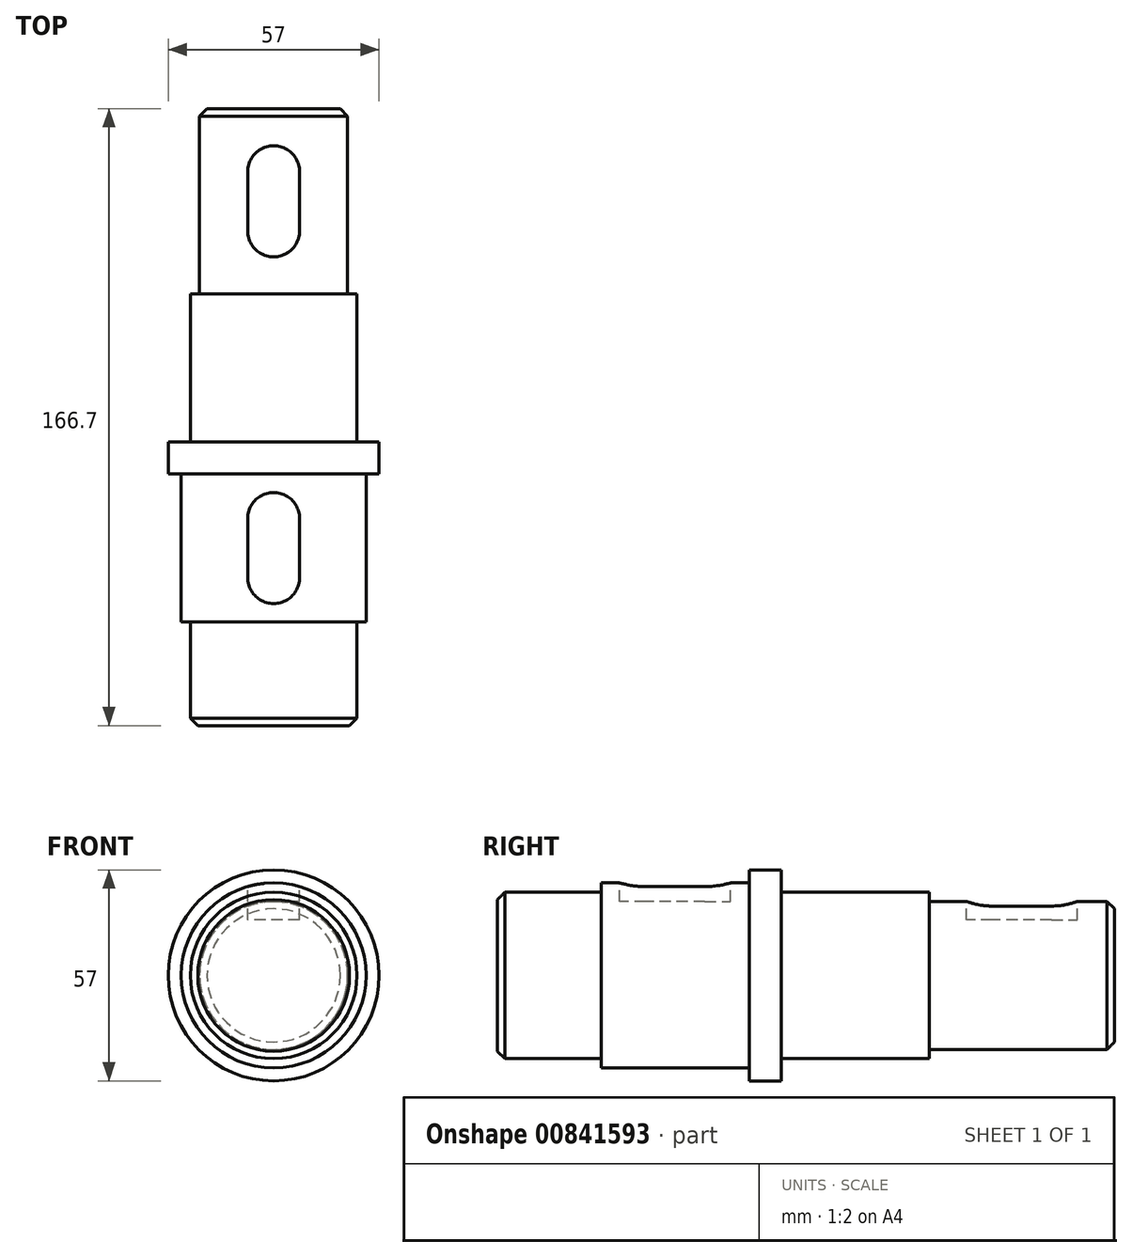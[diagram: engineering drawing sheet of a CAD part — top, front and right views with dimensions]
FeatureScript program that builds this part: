
annotation { "Feature Type Name" : "Feature", "Feature Type Description" : "" }
export const myFeature = defineFeature(function(context is Context, id is Id, definition is map)
    precondition{}
    {
        {
            var Q0;
            Q0=qCreatedBy(makeId("Top.planeOp"),FACE);
            var sketch = newSketch(context, id + "F0", { "sketchPlane" : qUnion([Q0])});
            skLineSegment(sketch, "E0", {"start": v(0, 0) * mm, "end": v(-22.5, 0) * mm});
            skLineSegment(sketch, "E1", {"start": v(-22.5, 0) * mm, "end": v(-22.5, 28) * mm});
            skLineSegment(sketch, "E2", {"start": v(-22.5, 28) * mm, "end": v(-25, 28) * mm});
            skLineSegment(sketch, "E3", {"start": v(-25, 28) * mm, "end": v(-25, 68) * mm});
            skLineSegment(sketch, "E4", {"start": v(-25, 68) * mm, "end": v(-28.5, 68) * mm});
            skLineSegment(sketch, "E5", {"start": v(-28.5, 68) * mm, "end": v(-28.5, 76.7) * mm});
            skLineSegment(sketch, "E6", {"start": v(-28.5, 76.7) * mm, "end": v(-22.5, 76.7) * mm});
            skLineSegment(sketch, "E7", {"start": v(-20, 116.7) * mm, "end": v(-20, 166.7) * mm});
            skLineSegment(sketch, "E8", {"start": v(-20, 166.7) * mm, "end": v(0, 166.7) * mm});
            skLineSegment(sketch, "E9", {"start": v(0, 166.7) * mm, "end": v(0, 0) * mm});
            skLineSegment(sketch, "E10", {"start": v(0, 166.7) * mm, "end": v(0, -47.12) * mm, "construction": true});
            skLineSegment(sketch, "E11", {"start": v(-22.5, 76.7) * mm, "end": v(-22.5, 116.7) * mm});
            skLineSegment(sketch, "E12", {"start": v(-22.5, 116.7) * mm, "end": v(-20, 116.7) * mm});
            skSolve(sketch);
        }
        {
            var Q0;
            Q0 = qSketchRegion(id + "F0", true);
            var Q1;
            Q1=sQuery(id+"F0.wireOp",EDGE,"E10");
            revolve(context, id + "F1", {"surfaceOperationType" : NewSurfaceOperationType.NEW, "entities" : qUnion([Q0]), "axis" : qUnion([Q1]), "revolveType" : RevolveType.FULL});
        }
        {
            var Q0;
            Q0=makeQuery(id+"F1.opRevolve","SWEPT_EDGE",EDGE,{"disambiguationData":[OSD([sQuery(id+"F0.wireOp",EDGE,"E7"),sQuery(id+"F0.wireOp",EDGE,"E8")])]});
            var Q1;
            Q1=makeQuery(id+"F1.opRevolve","SWEPT_EDGE",EDGE,{"disambiguationData":[OSD([sQuery(id+"F0.wireOp",EDGE,"E0"),sQuery(id+"F0.wireOp",EDGE,"E1")])]});
            chamfer(context, id + "F2", {"entities" : qUnion([Q0, Q1]), "width" : 2 * mm, "tangentPropagation" : true});
        }
        {
            var Q0;
            Q0=qCreatedBy(makeId("Top.planeOp"),FACE);
            cPlane(context, id + "F3", {"entities" : qUnion([Q0]), "cplaneType" : CPlaneType.OFFSET, "offset" : 25 * mm, "width" : 150 * mm, "height" : 150 * mm});
        }
        {
            var Q0;
            Q0=qCreatedBy(id+"F3.planeOp",FACE);
            var sketch = newSketch(context, id + "F4", { "sketchPlane" : qUnion([Q0])});
            skLineSegment(sketch, "E13.bottom", {"start": v(0, 63) * mm, "end": v(0, 63) * mm});
            skLineSegment(sketch, "E13.top", {"start": v(0, 33) * mm, "end": v(0, 33) * mm});
            skLineSegment(sketch, "E13.left", {"start": v(7, 56) * mm, "end": v(7, 40) * mm});
            skLineSegment(sketch, "E13.right", {"start": v(-7, 56) * mm, "end": v(-7, 40) * mm});
            skPoint(sketch, "E13.middle", {"position": v(0, 48) * mm});
            skPoint(sketch, "E14.visualSharp", {"position": v(-7, 63) * mm});
            skArc(sketch, "E14.filletArc", {"start": v(0, 63) * mm, "mid": v(-4.95, 60.95) * mm, "end": v(-7, 56) * mm});
            skPoint(sketch, "E15.visualSharp", {"position": v(7, 63) * mm});
            skArc(sketch, "E15.filletArc", {"start": v(7, 56) * mm, "mid": v(4.95, 60.95) * mm, "end": v(0, 63) * mm});
            skPoint(sketch, "E16.visualSharp", {"position": v(-7, 33) * mm});
            skArc(sketch, "E16.filletArc", {"start": v(-7, 40) * mm, "mid": v(-4.95, 35.05) * mm, "end": v(0, 33) * mm});
            skPoint(sketch, "E17.visualSharp", {"position": v(7, 33) * mm});
            skArc(sketch, "E17.filletArc", {"start": v(0, 33) * mm, "mid": v(4.95, 35.05) * mm, "end": v(7, 40) * mm});
            skLineSegment(sketch, "E18.bottom", {"start": v(0, 156.7) * mm, "end": v(0, 156.7) * mm});
            skLineSegment(sketch, "E18.top", {"start": v(0, 126.7) * mm, "end": v(0, 126.7) * mm});
            skLineSegment(sketch, "E18.left", {"start": v(7, 149.7) * mm, "end": v(7, 133.7) * mm});
            skLineSegment(sketch, "E18.right", {"start": v(-7, 149.7) * mm, "end": v(-7, 133.7) * mm});
            skPoint(sketch, "E18.middle", {"position": v(0, 141.7) * mm});
            skPoint(sketch, "E19.visualSharp", {"position": v(-7, 156.7) * mm});
            skArc(sketch, "E19.filletArc", {"start": v(0, 156.7) * mm, "mid": v(-4.95, 154.65) * mm, "end": v(-7, 149.7) * mm});
            skPoint(sketch, "E20.visualSharp", {"position": v(7, 156.7) * mm});
            skArc(sketch, "E20.filletArc", {"start": v(7, 149.7) * mm, "mid": v(4.95, 154.65) * mm, "end": v(0, 156.7) * mm});
            skPoint(sketch, "E21.visualSharp", {"position": v(7, 126.7) * mm});
            skArc(sketch, "E21.filletArc", {"start": v(0, 126.7) * mm, "mid": v(4.95, 128.75) * mm, "end": v(7, 133.7) * mm});
            skPoint(sketch, "E22.visualSharp", {"position": v(-7, 126.7) * mm});
            skArc(sketch, "E22.filletArc", {"start": v(-7, 133.7) * mm, "mid": v(-4.95, 128.75) * mm, "end": v(0, 126.7) * mm});
            skSolve(sketch);
        }
        {
            var Q0;
            Q0=makeQuery(id+"F4.imprint","IMPRINT",FACE,{"disambiguationData":[TD([[makeQuery(id+"F4.imprint","IMPRINT",EDGE,{"derivedFrom":sQuery(id+"F4.wireOp",EDGE,"E13.left")}),-1.0]])]});
            extrude(context, id + "F5", {"entities" : qUnion([Q0]), "operationType" : NewBodyOperationType.REMOVE, "oppositeDirection" : true, "depth" : 5 * mm, "offsetDistance" : 25 * mm});
        }
        {
            var Q0;
            Q0=makeQuery(id+"F4.imprint","IMPRINT",FACE,{"disambiguationData":[TD([[makeQuery(id+"F4.imprint","IMPRINT",EDGE,{"derivedFrom":sQuery(id+"F4.wireOp",EDGE,"E18.left")}),-1.0]])]});
            extrude(context, id + "F6", {"entities" : qUnion([Q0]), "operationType" : NewBodyOperationType.REMOVE, "oppositeDirection" : true, "depth" : 10 * mm, "offsetDistance" : 25 * mm});
        }
    });
